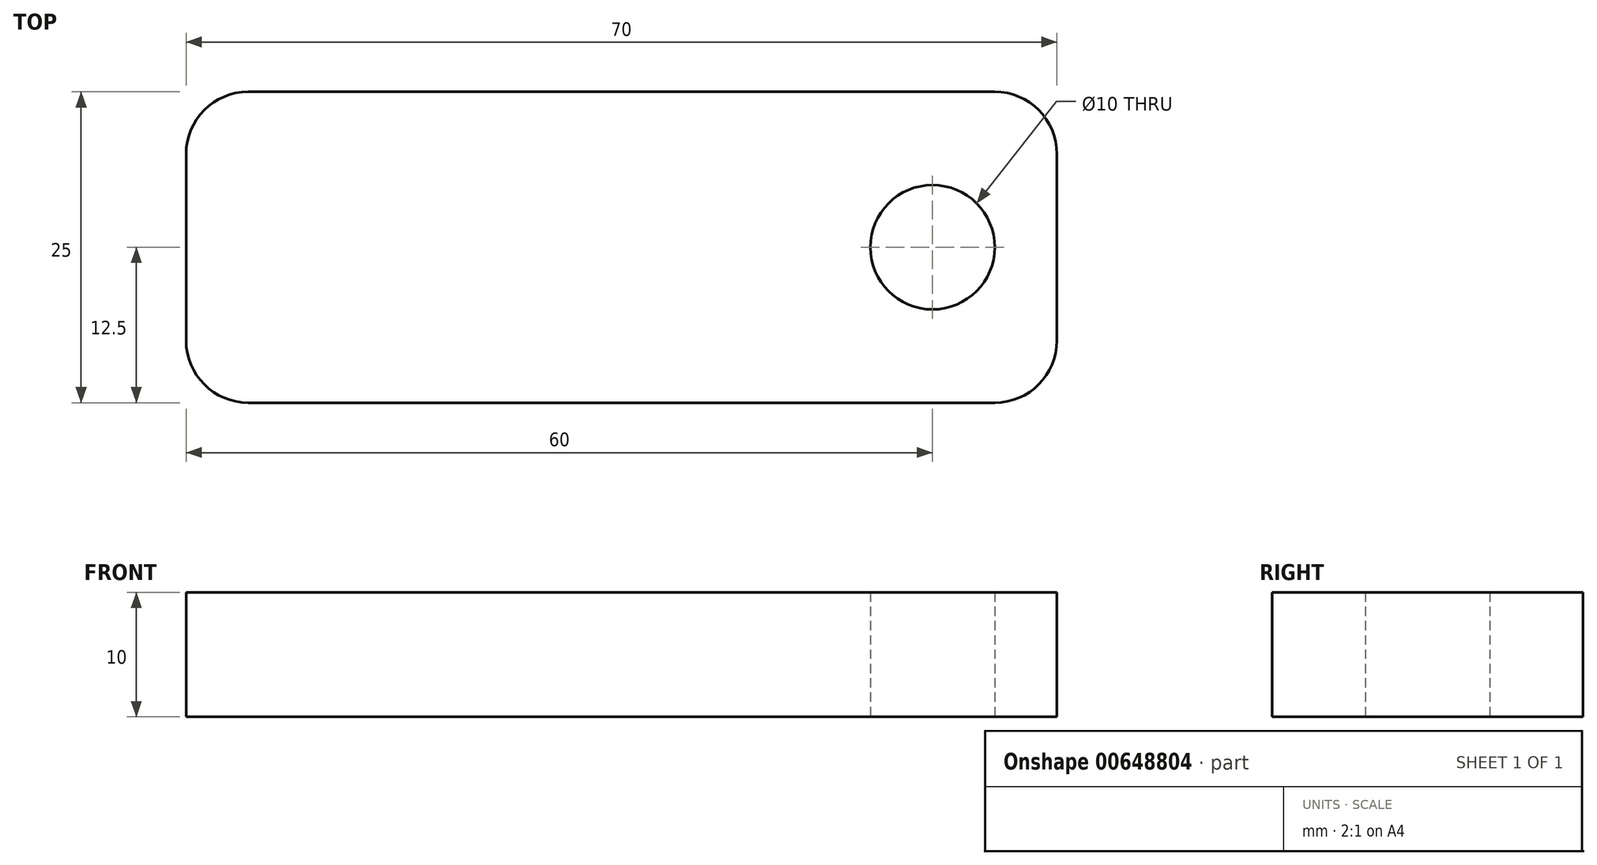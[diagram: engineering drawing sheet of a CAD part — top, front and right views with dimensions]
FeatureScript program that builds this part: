
annotation { "Feature Type Name" : "Feature", "Feature Type Description" : "" }
export const myFeature = defineFeature(function(context is Context, id is Id, definition is map)
    precondition{}
    {
        {
            var Q0;
            Q0=qCreatedBy(makeId("Top.planeOp"),FACE);
            var sketch = newSketch(context, id + "F0", { "sketchPlane" : qUnion([Q0])});
            skLineSegment(sketch, "E0.bottom", {"start": v(35, 12.5) * mm, "end": v(-35, 12.5) * mm});
            skLineSegment(sketch, "E0.top", {"start": v(35, -12.5) * mm, "end": v(-35, -12.5) * mm});
            skLineSegment(sketch, "E0.left", {"start": v(35, 12.5) * mm, "end": v(35, -12.5) * mm});
            skLineSegment(sketch, "E0.right", {"start": v(-35, 12.5) * mm, "end": v(-35, -12.5) * mm});
            skPoint(sketch, "E0.middle", {"position": v(0, 0) * mm});
            skCircle(sketch, "E1", {"center": v(25, 0) * mm, "radius": 5 * mm});
            skSolve(sketch);
        }
        {
            var Q0;
            Q0=makeQuery(id+"F0.imprint","IMPRINT",FACE,{"disambiguationData":[TD([[makeQuery(id+"F0.imprint","IMPRINT",EDGE,{"derivedFrom":sQuery(id+"F0.wireOp",EDGE,"E0.bottom")}),1.0]])]});
            extrude(context, id + "F1", {"entities" : qUnion([Q0]), "depth" : 10 * mm, "offsetDistance" : 25 * mm});
        }
        {
            var Q0;
            Q0=makeQuery(id+"F1.opExtrude","SWEPT_EDGE",EDGE,{"disambiguationData":[OSD([sQuery(id+"F0.wireOp",EDGE,"E0.top"),sQuery(id+"F0.wireOp",EDGE,"E0.right")])]});
            var Q1;
            Q1=makeQuery(id+"F1.opExtrude","SWEPT_EDGE",EDGE,{"disambiguationData":[OSD([sQuery(id+"F0.wireOp",EDGE,"E0.bottom"),sQuery(id+"F0.wireOp",EDGE,"E0.right")])]});
            var Q2;
            Q2=makeQuery(id+"F1.opExtrude","SWEPT_EDGE",EDGE,{"disambiguationData":[OSD([sQuery(id+"F0.wireOp",EDGE,"E0.top"),sQuery(id+"F0.wireOp",EDGE,"E0.left")])]});
            var Q3;
            Q3=makeQuery(id+"F1.opExtrude","SWEPT_EDGE",EDGE,{"disambiguationData":[OSD([sQuery(id+"F0.wireOp",EDGE,"E0.bottom"),sQuery(id+"F0.wireOp",EDGE,"E0.left")])]});
            fillet(context, id + "F2", {"entities" : qUnion([Q0, Q1, Q2, Q3]), "radius" : 5 * mm, "tangentPropagation" : true, "allowEdgeOverflow" : false});
        }
    });
